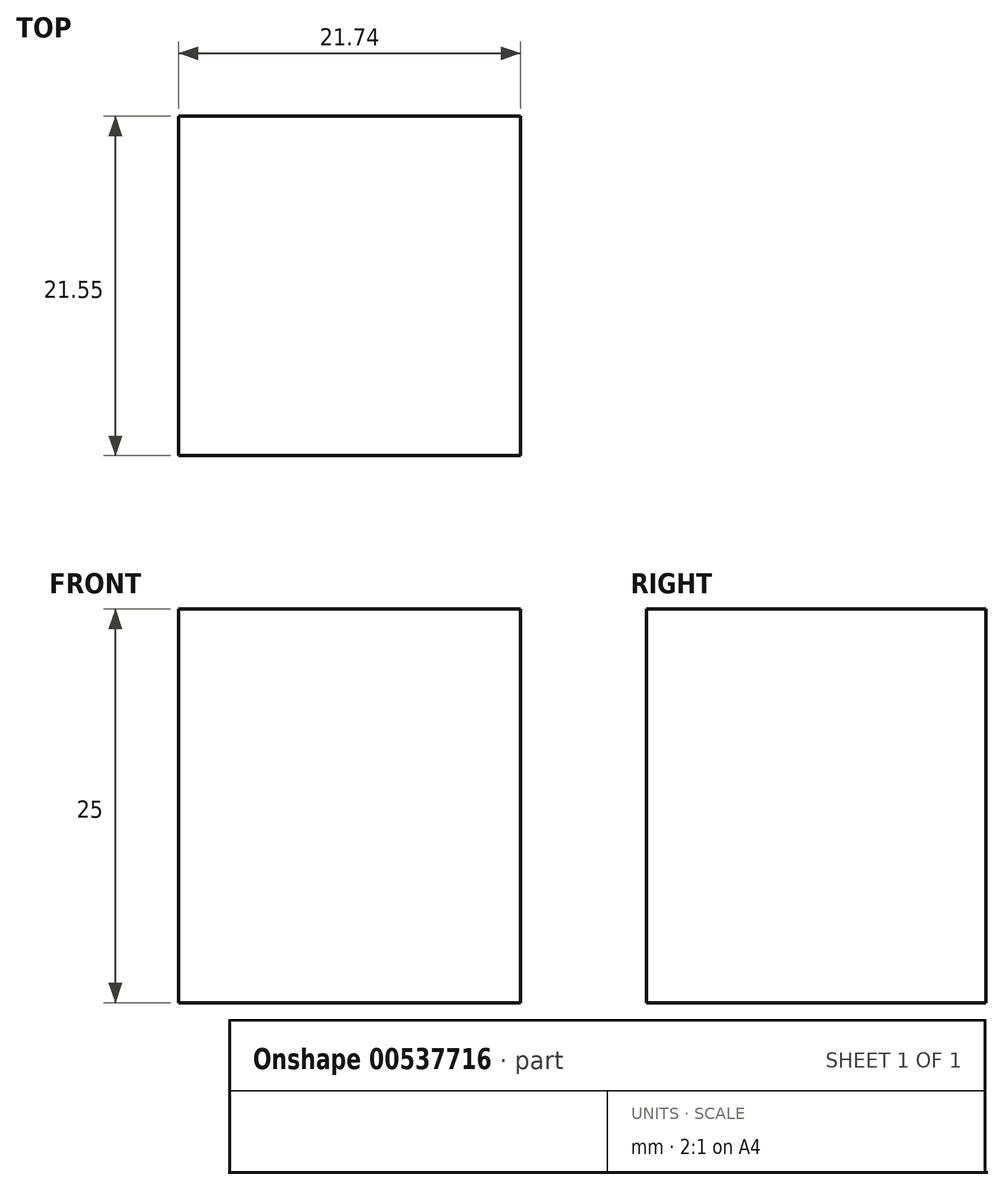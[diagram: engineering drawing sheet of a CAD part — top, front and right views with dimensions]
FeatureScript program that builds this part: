
annotation { "Feature Type Name" : "Feature", "Feature Type Description" : "" }
export const myFeature = defineFeature(function(context is Context, id is Id, definition is map)
    precondition{}
    {
        {
            var Q0;
            Q0=qCreatedBy(makeId("Top.planeOp"),FACE);
            var sketch = newSketch(context, id + "F0", { "sketchPlane" : qUnion([Q0])});
            skLineSegment(sketch, "E0.bottom", {"start": v(0, 0) * mm, "end": v(21.74, 0) * mm});
            skLineSegment(sketch, "E0.top", {"start": v(0, 21.55) * mm, "end": v(21.74, 21.55) * mm});
            skLineSegment(sketch, "E0.left", {"start": v(0, 0) * mm, "end": v(0, 21.55) * mm});
            skLineSegment(sketch, "E0.right", {"start": v(21.74, 0) * mm, "end": v(21.74, 21.55) * mm});
            skSolve(sketch);
        }
        {
            var Q0;
            Q0=makeQuery(id+"F0.imprint","IMPRINT",FACE,{"disambiguationData":[TD([[makeQuery(id+"F0.imprint","IMPRINT",EDGE,{"derivedFrom":sQuery(id+"F0.wireOp",EDGE,"E0.bottom")}),1.0]])]});
            extrude(context, id + "F1", {"entities" : qUnion([Q0]), "depth" : 25 * mm, "offsetDistance" : 25 * mm});
        }
    });
